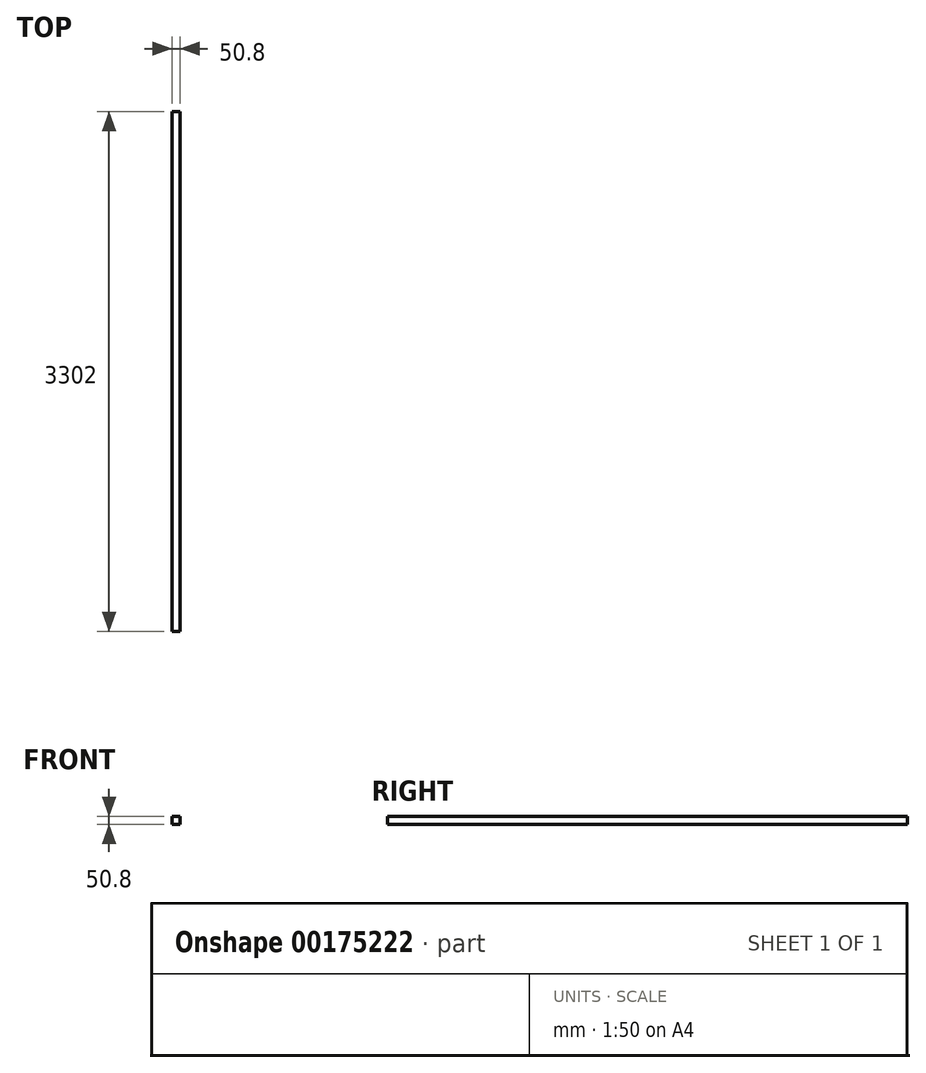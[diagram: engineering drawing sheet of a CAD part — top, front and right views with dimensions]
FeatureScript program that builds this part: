
annotation { "Feature Type Name" : "Feature", "Feature Type Description" : "" }
export const myFeature = defineFeature(function(context is Context, id is Id, definition is map)
    precondition{}
    {
        {
            var Q0;
            Q0=qCreatedBy(makeId("Front.planeOp"),FACE);
            var sketch = newSketch(context, id + "F0", { "sketchPlane" : qUnion([Q0])});
            skLineSegment(sketch, "E0.bottom", {"start": v(25.4, 25.4) * mm, "end": v(-25.4, 25.4) * mm});
            skLineSegment(sketch, "E0.top", {"start": v(25.4, -25.4) * mm, "end": v(-25.4, -25.4) * mm});
            skLineSegment(sketch, "E0.left", {"start": v(25.4, 25.4) * mm, "end": v(25.4, -25.4) * mm});
            skLineSegment(sketch, "E0.right", {"start": v(-25.4, 25.4) * mm, "end": v(-25.4, -25.4) * mm});
            skPoint(sketch, "E0.middle", {"position": v(0, 0) * mm});
            skSolve(sketch);
        }
        {
            var Q0;
            Q0 = qSketchRegion(id + "F0", true);
            extrude(context, id + "F1", {"entities" : qUnion([Q0]), "endBound" : BoundingType.SYMMETRIC, "depth" : 3302 * mm});
        }
    });
